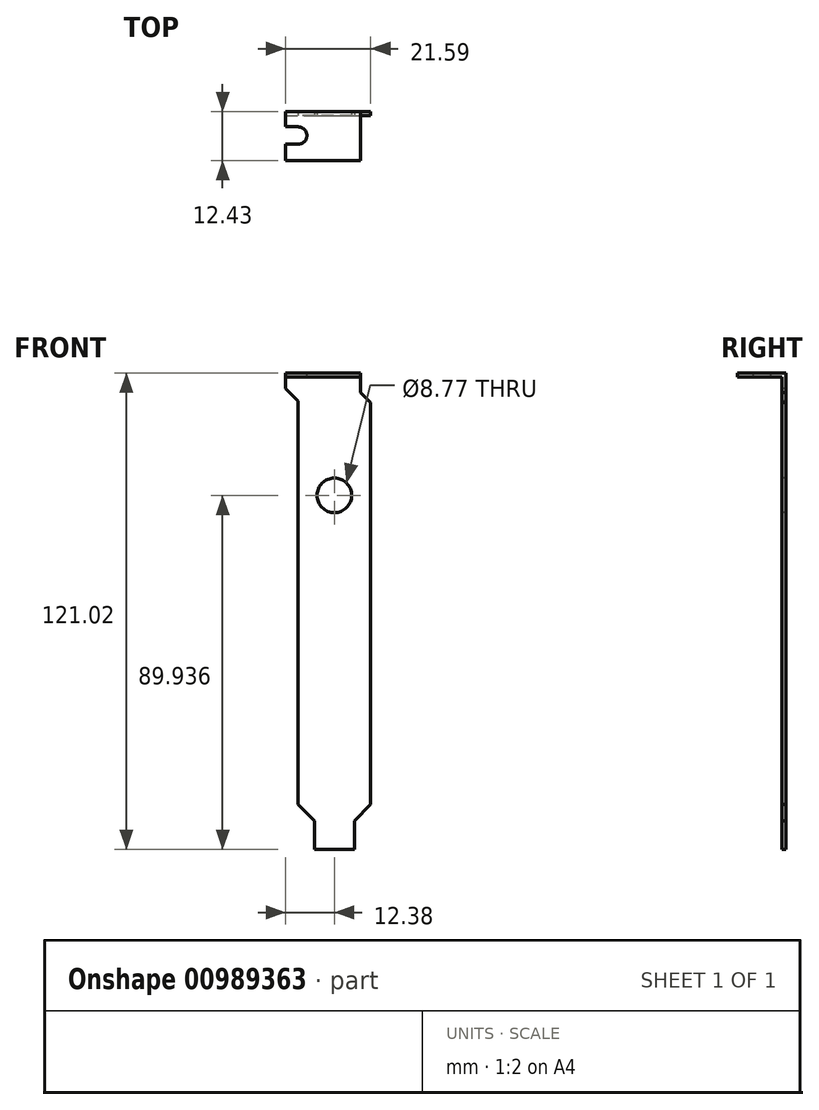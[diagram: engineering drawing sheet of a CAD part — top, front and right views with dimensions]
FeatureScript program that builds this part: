
annotation { "Feature Type Name" : "Feature", "Feature Type Description" : "" }
export const myFeature = defineFeature(function(context is Context, id is Id, definition is map)
    precondition{}
    {
        {
            assignVariable(context, id + "F0", {"name" : "BracketThickness", "anyValue" : 1 * mm});
        }
        {
            var Q0;
            Q0=qCreatedBy(makeId("Front.planeOp"),FACE);
            var sketch = newSketch(context, id + "F1", { "sketchPlane" : qUnion([Q0])});
            skLineSegment(sketch, "E0", {"start": v(-5.1, 0) * mm, "end": v(5.1, 0) * mm});
            skLineSegment(sketch, "E1", {"start": v(-5.1, 0) * mm, "end": v(-5.1, 7.27) * mm});
            skLineSegment(sketch, "E2", {"start": v(5.1, 0) * mm, "end": v(5.1, 7.27) * mm});
            skLineSegment(sketch, "E3", {"start": v(5.1, 7.27) * mm, "end": v(-5.1, 7.27) * mm, "construction": true});
            skLineSegment(sketch, "E4", {"start": v(-5.1, 7.27) * mm, "end": v(-9.21, 11.38) * mm});
            skLineSegment(sketch, "E5", {"start": v(-9.21, 11.38) * mm, "end": v(-9.21, 113.93) * mm});
            skLineSegment(sketch, "E6", {"start": v(5.1, 7.27) * mm, "end": v(9.2, 11.38) * mm});
            skLineSegment(sketch, "E7", {"start": v(9.2, 11.38) * mm, "end": v(9.2, 113.54) * mm});
            skLineSegment(sketch, "E8", {"start": v(9.21, 113.54) * mm, "end": v(6.67, 116.08) * mm});
            skLineSegment(sketch, "E9", {"start": v(6.67, 116.08) * mm, "end": v(6.67, 120.02) * mm});
            skLineSegment(sketch, "E10", {"start": v(6.67, 120.02) * mm, "end": v(-12.38, 120.02) * mm, "construction": true});
            skLineSegment(sketch, "E11", {"start": v(-12.38, 120.02) * mm, "end": v(-12.38, 117.1) * mm});
            skLineSegment(sketch, "E12", {"start": v(-12.38, 117.1) * mm, "end": v(-9.21, 113.93) * mm});
            skLineSegment(sketch, "E13", {"start": v(-9.21, 11.38) * mm, "end": v(9.2, 11.38) * mm, "construction": true});
            skLineSegment(sketch, "E14", {"start": v(-12.38, 120.02) * mm, "end": v(-12.38, 121.02) * mm});
            skLineSegment(sketch, "E15", {"start": v(-12.38, 121.02) * mm, "end": v(6.67, 121.02) * mm});
            skLineSegment(sketch, "E16", {"start": v(6.67, 121.02) * mm, "end": v(6.67, 120.02) * mm});
            skCircle(sketch, "E17", {"center": v(0, 89.94) * mm, "radius": 4.38 * mm});
            skSolve(sketch);
        }
        {
            var Q0;
            Q0=makeQuery(id+"F1.imprint","IMPRINT",FACE,{"disambiguationData":[TD([[makeQuery(id+"F1.imprint","IMPRINT",EDGE,{"derivedFrom":sQuery(id+"F1.wireOp",EDGE,"E0")}),1.0]])]});
            extrude(context, id + "F2", {"entities" : qUnion([Q0]), "oppositeDirection" : true, "depth" : getVariable(context, 'BracketThickness')});
        }
        {
            var Q0;
            Q0=makeQuery(id+"F2.opExtrude","SWEPT_FACE",FACE,{"disambiguationData":[OSD([sQuery(id+"F1.wireOp",EDGE,"E15")])]});
            var sketch = newSketch(context, id + "F3", { "sketchPlane" : qUnion([Q0])});
            skLineSegment(sketch, "E18.bottom", {"start": v(-12.38, 0) * mm, "end": v(6.67, 0) * mm});
            skLineSegment(sketch, "E18.top", {"start": v(-12.38, -11.43) * mm, "end": v(6.67, -11.43) * mm});
            skLineSegment(sketch, "E18.left", {"start": v(-12.38, 0) * mm, "end": v(-12.38, -11.43) * mm});
            skLineSegment(sketch, "E18.right", {"start": v(6.67, 0) * mm, "end": v(6.67, -11.43) * mm});
            skLineSegment(sketch, "E19", {"start": v(-12.38, -2.87) * mm, "end": v(-9.2, -2.87) * mm});
            skLineSegment(sketch, "E20", {"start": v(-9.2, -2.87) * mm, "end": v(-9.2, -7.3) * mm, "construction": true});
            skLineSegment(sketch, "E21", {"start": v(-9.2, -7.3) * mm, "end": v(-12.38, -7.3) * mm});
            skArc(sketch, "E22", {"start": v(-9.2, -2.87) * mm, "mid": v(-7, -5.08) * mm, "end": v(-9.2, -7.3) * mm});
            skSolve(sketch);
        }
        {
            var Q0;
            {var subQ1=sQuery(id+"F3.wireOp",EDGE,"E18.bottom");Q0=makeQuery(id+"F3.imprint","IMPRINT",FACE,{"disambiguationData":[TD([[makeQuery(id+"F3.imprint","IMPRINT",EDGE,{"derivedFrom":subQ1}),-1.0]])]});}
            extrude(context, id + "F4", {"entities" : qUnion([Q0]), "operationType" : NewBodyOperationType.ADD, "oppositeDirection" : true, "depth" : getVariable(context, 'BracketThickness')});
        }
    });
